# Revit family: КПДУ
name_source: partatom
category: Арматура воздуховодов
units: mm (PartAtom-declared; Revit-internal decimal feet)

## family parameters
Всегда вертикально = Да
На основе рабочей плоскости = Нет
Общий = Нет
При загрузке вырезать с полостями = Нет
Размер круглого соединителя = Использовать диаметр
Тип детали = Присоединяется

## types (184) — shared parameters
00_20_Manufacturer = Вентс
00_20_Name = Клапан протипожежний димовий
Grid Material = Cover Grid Cross
Load Classification = HVAC
Maintenance zone material = <По категории>
Maximum Air Flow = 0.0 л/с
zero-valued in all types: Отметка по умолчанию

## per-type parameters (varying)
| type | 00_20_Type | B | B1 | B2 | B3 | Bn | H | H1 | H2 | H3 | Hn | Power | Voltage | Вес | Два фланца | Количество створок | Размещение привода (внутри) | Размещение привода (снаружи) |
| КПДУ-300х300-2-ПВ24-СН | КПДУ-300х300-2-ПВ24-СН | 300 мм | 320 мм | 340 мм | 160 мм | 310 мм | 300 мм | 320 мм | 340 мм | 50 мм | 310 мм | 9 В·А | 24 В | 6.5 кг | Да | 1 | Нет | Да |
| КПДУ-1400х1400-2-ПВ24-СН | КПДУ-1400х1400-2-ПВ24-СН | 1400 мм | 1430 мм | 1460 мм | 715 мм | 1410 мм | 1400 мм | 1430 мм | 1460 мм | 600 мм | 1410 мм | 18 В·А | 24 В | 52 кг | Да | 5 | Нет | Да |
| КПДУ-300х300-1-ПВ24-СН | КПДУ-300х300-1-ПВ24-СН | 300 мм | 320 мм | 340 мм | 160 мм | 310 мм | 300 мм | 320 мм | 340 мм | 50 мм | 310 мм | 9 В·А | 24 В | 6.5 кг | Нет | 1 | Нет | Да |
| КПДУ-1400х1400-1-ПВ24-СН | КПДУ-1400х1400-1-ПВ24-СН | 1400 мм | 1430 мм | 1460 мм | 715 мм | 1410 мм | 1400 мм | 1430 мм | 1460 мм | 600 мм | 1410 мм | 18 В·А | 24 В | 52 кг | Нет | 5 | Нет | Да |
| КПДУ-300х300-1-ПВ24-ВН | КПДУ-300х300-1-ПВ24-ВН | 300 мм | 320 мм | 340 мм | 160 мм | 310 мм | 300 мм | 320 мм | 340 мм | 50 мм | 310 мм | 9 В·А | 24 В | 6.5 кг | Нет | 1 | Да | Нет |
| КПДУ-300х300-2-ПВ24-ВН | КПДУ-300х300-2-ПВ24-ВН | 300 мм | 320 мм | 340 мм | 160 мм | 310 мм | 300 мм | 320 мм | 340 мм | 50 мм | 310 мм | 9 В·А | 24 В | 6.5 кг | Да | 1 | Да | Нет |
| КПДУ-1400х1400-1-ПВ24-ВН | КПДУ-1400х1400-1-ПВ24-ВН | 1400 мм | 1430 мм | 1460 мм | 715 мм | 1410 мм | 1400 мм | 1430 мм | 1460 мм | 600 мм | 1410 мм | 18 В·А | 24 В | 52 кг | Нет | 5 | Да | Нет |
| КПДУ-1400х1400-2-ПВ24-ВН | КПДУ-1400х1400-2-ПВ24-ВН | 1400 мм | 1430 мм | 1460 мм | 715 мм | 1410 мм | 1400 мм | 1430 мм | 1460 мм | 600 мм | 1410 мм | 18 В·А | 24 В | 52 кг | Да | 5 | Да | Нет |
| КПДУ-300х300-1-ПВ230-ВН | КПДУ-300х300-1-ПВ230-ВН | 300 мм | 320 мм | 340 мм | 160 мм | 310 мм | 300 мм | 320 мм | 340 мм | 50 мм | 310 мм | 12 В·А | 230 В | 6.5 кг | Нет | 1 | Да | Нет |
| КПДУ-300х300-1-ПВ230-СН | КПДУ-300х300-1-ПВ230-СН | 300 мм | 320 мм | 340 мм | 160 мм | 310 мм | 300 мм | 320 мм | 340 мм | 50 мм | 310 мм | 12 В·А | 230 В | 6.5 кг | Нет | 1 | Нет | Да |
| КПДУ-300х300-2-ПВ230-ВН | КПД-300х300-2-ПВ230-ВН | 300 мм | 320 мм | 340 мм | 160 мм | 310 мм | 300 мм | 320 мм | 340 мм | 50 мм | 310 мм | 12 В·А | 230 В | 6.5 кг | Да | 1 | Да | Нет |
| КПДУ-300х300-2-ПВ230-СН | КПДУ-300х300-2-ПВ230-СН | 300 мм | 320 мм | 340 мм | 160 мм | 310 мм | 300 мм | 320 мм | 340 мм | 50 мм | 310 мм | 12 В·А | 230 В | 6.5 кг | Да | 1 | Нет | Да |
| КПДУ-1400х1400-1-ПВ230-ВН | КПДУ-1400х1400-1-ПВ230-ВН | 1400 мм | 1430 мм | 1460 мм | 715 мм | 1410 мм | 1400 мм | 1430 мм | 1460 мм | 600 мм | 1410 мм | 15 В·А | 230 В | 52 кг | Нет | 5 | Да | Нет |
| КПДУ-1400х1400-1-ПВ230-СН | КПДУ-1400х1400-1-ПВ230-СН | 1400 мм | 1430 мм | 1460 мм | 715 мм | 1410 мм | 1400 мм | 1430 мм | 1460 мм | 600 мм | 1410 мм | 15 В·А | 230 В | 52 кг | Нет | 5 | Нет | Да |
| КПДУ-1400х1400-2-ПВ230-ВН | КПДУ-1400х1400-2-ПВ230-ВН | 1400 мм | 1430 мм | 1460 мм | 715 мм | 1410 мм | 1400 мм | 1430 мм | 1460 мм | 600 мм | 1410 мм | 15 В·А | 230 В | 52 кг | Да | 5 | Да | Нет |
| КПДУ-1400х1400-2-ПВ230-СН | КПДУ-1400х1400-2-ПВ230-СН | 1400 мм | 1430 мм | 1460 мм | 715 мм | 1410 мм | 1400 мм | 1430 мм | 1460 мм | 600 мм | 1410 мм | 15 В·А | 230 В | 52 кг | Да | 5 | Нет | Да |
| КПДУ-350х350-1-ПВ230-ВН | КПДУ-350х350-1-ПВ230-ВН | 350 мм | 370 мм | 390 мм | 185 мм | 360 мм | 350 мм | 370 мм | 390 мм | 75 мм | 360 мм | 12 В·А | 230 В | 7.8 кг | Нет | 1 | Да | Нет |
| КПДУ-350х350-1-ПВ230-СН | КПДУ-350х350-1-ПВ230-СН | 350 мм | 370 мм | 390 мм | 185 мм | 360 мм | 350 мм | 370 мм | 390 мм | 75 мм | 360 мм | 12 В·А | 230 В | 7.8 кг | Нет | 1 | Нет | Да |
| КПДУ-350х350-1-ПВ24-ВН | КПДУ-350х350-1-ПВ24-ВН | 350 мм | 370 мм | 390 мм | 185 мм | 360 мм | 350 мм | 370 мм | 390 мм | 75 мм | 360 мм | 9 В·А | 24 В | 7.8 кг | Нет | 1 | Да | Нет |
| КПДУ-350х350-1-ПВ24-СН | КПДУ-350х350-1-ПВ24-СН | 350 мм | 370 мм | 390 мм | 185 мм | 360 мм | 350 мм | 370 мм | 390 мм | 75 мм | 360 мм | 9 В·А | 24 В | 7.8 кг | Нет | 1 | Нет | Да |
| КПДУ-350х350-2-ПВ230-ВН | КПДУ-350х350-2-ПВ230-ВН | 350 мм | 370 мм | 390 мм | 185 мм | 360 мм | 350 мм | 370 мм | 390 мм | 75 мм | 360 мм | 12 В·А | 230 В | 7.8 кг | Да | 1 | Да | Нет |
| КПДУ-350х350-2-ПВ230-СН | КПДУ-350х350-2-ПВ230-СН | 350 мм | 370 мм | 390 мм | 185 мм | 360 мм | 350 мм | 370 мм | 390 мм | 75 мм | 360 мм | 12 В·А | 230 В | 7.8 кг | Да | 1 | Нет | Да |
| КПДУ-350х350-2-ПВ24-ВН | КПДУ-350х350-2-ПВ24-ВН | 350 мм | 370 мм | 390 мм | 185 мм | 360 мм | 350 мм | 370 мм | 390 мм | 75 мм | 360 мм | 9 В·А | 24 В | 7.8 кг | Да | 1 | Да | Нет |
| КПДУ-350х350-2-ПВ24-СН | КПДУ-350х350-2-ПВ24-СН | 350 мм | 370 мм | 390 мм | 185 мм | 360 мм | 350 мм | 370 мм | 390 мм | 75 мм | 360 мм | 9 В·А | 24 В | 7.8 кг | Да | 1 | Нет | Да |
| КПДУ-400х400-1-ПВ230-ВН | КПДУ-400х400-1-ПВ230-ВН | 400 мм | 420 мм | 440 мм | 210 мм | 410 мм | 400 мм | 420 мм | 440 мм | 100 мм | 410 мм | 12 В·А | 230 В | 9.5 кг | Нет | 2 | Да | Нет |
| КПДУ-400х400-1-ПВ230-СН | КПДУ-400х400-1-ПВ230-СН | 400 мм | 420 мм | 440 мм | 210 мм | 410 мм | 400 мм | 420 мм | 440 мм | 100 мм | 410 мм | 12 В·А | 230 В | 9.5 кг | Нет | 2 | Нет | Да |
| КПДУ-400х400-1-ПВ24-СН | КПДУ-400х400-1-ПВ24-СН | 400 мм | 420 мм | 440 мм | 210 мм | 410 мм | 400 мм | 420 мм | 440 мм | 100 мм | 410 мм | 9 В·А | 24 В | 9.5 кг | Нет | 2 | Нет | Да |
| КПДУ-400х400-1-ПВ24-ВН | КПДУ-400х400-1-ПВ24-ВН | 400 мм | 420 мм | 440 мм | 210 мм | 410 мм | 400 мм | 420 мм | 440 мм | 100 мм | 410 мм | 9 В·А | 24 В | 9.5 кг | Нет | 2 | Да | Нет |
| КПДУ-400х400-2-ПВ230-ВН | КПДУ-400х400-2-ПВ230-ВН | 400 мм | 420 мм | 440 мм | 210 мм | 410 мм | 400 мм | 420 мм | 440 мм | 100 мм | 410 мм | 12 В·А | 230 В | 9.5 кг | Да | 2 | Да | Нет |
| КПДУ-400х400-2-ПВ230-СН | КПДУ-400х400-2-ПВ230-СН | 400 мм | 420 мм | 440 мм | 210 мм | 410 мм | 400 мм | 420 мм | 440 мм | 100 мм | 410 мм | 12 В·А | 230 В | 9.5 кг | Да | 2 | Нет | Да |
| КПДУ-400х400-2-ПВ24-ВН | КПДУ-400х400-2-ПВ24-ВН | 400 мм | 420 мм | 440 мм | 210 мм | 410 мм | 400 мм | 420 мм | 440 мм | 100 мм | 410 мм | 9 В·А | 24 В | 9.5 кг | Да | 2 | Да | Нет |
| КПДУ-400х400-2-ПВ24-СН | КПДУ-400х400-2-ПВ24-СН | 400 мм | 420 мм | 440 мм | 210 мм | 410 мм | 400 мм | 420 мм | 440 мм | 100 мм | 410 мм | 9 В·А | 24 В | 9.5 кг | Да | 2 | Нет | Да |
| КПДУ-450х450-1-ПВ230-ВН | КПДУ-450х450-1-ПВ230-ВН | 450 мм | 470 мм | 490 мм | 235 мм | 460 мм | 450 мм | 470 мм | 490 мм | 125 мм | 460 мм | 12 В·А | 230 В | 11.3 кг | Нет | 2 | Да | Нет |
| КПДУ-450х450-1-ПВ230-СН | КПДУ-450х450-1-ПВ230-СН | 450 мм | 470 мм | 490 мм | 235 мм | 460 мм | 450 мм | 470 мм | 490 мм | 125 мм | 460 мм | 12 В·А | 230 В | 11.3 кг | Нет | 2 | Нет | Да |
| КПДУ-450х450-1-ПВ24-ВН | КПДУ-450х450-1-ПВ24-ВН | 450 мм | 470 мм | 490 мм | 235 мм | 460 мм | 450 мм | 470 мм | 490 мм | 125 мм | 460 мм | 9 В·А | 24 В | 11.3 кг | Нет | 2 | Да | Нет |
| КПДУ-450х450-1-ПВ24-СН | КПДУ-450х450-1-ПВ24-СН | 450 мм | 470 мм | 490 мм | 235 мм | 460 мм | 450 мм | 470 мм | 490 мм | 125 мм | 460 мм | 9 В·А | 24 В | 11.3 кг | Нет | 2 | Нет | Да |
| КПДУ-450х450-2-ПВ230-ВН | КПДУ-450х450-2-ПВ230-ВН | 450 мм | 470 мм | 490 мм | 235 мм | 460 мм | 450 мм | 470 мм | 490 мм | 125 мм | 460 мм | 12 В·А | 230 В | 11.3 кг | Да | 2 | Да | Нет |
| КПДУ-450х450-2-ПВ230-СН | КПДУ-450х450-2-ПВ230-СН | 450 мм | 470 мм | 490 мм | 235 мм | 460 мм | 450 мм | 470 мм | 490 мм | 125 мм | 460 мм | 12 В·А | 230 В | 11.3 кг | Да | 2 | Нет | Да |
| КПДУ-450х450-2-ПВ24-ВН | КПДУ-450х450-2-ПВ24-ВН | 450 мм | 470 мм | 490 мм | 235 мм | 460 мм | 450 мм | 470 мм | 490 мм | 125 мм | 460 мм | 9 В·А | 24 В | 11.3 кг | Да | 2 | Да | Нет |
| КПДУ-450х450-2-ПВ24-СН | КПДУ-450х450-2-ПВ24-СН | 450 мм | 470 мм | 490 мм | 235 мм | 460 мм | 450 мм | 470 мм | 490 мм | 125 мм | 460 мм | 9 В·А | 24 В | 11.3 кг | Да | 2 | Нет | Да |
| КПДУ-500х500-1-ПВ230-ВН | КПДУ-500х500-1-ПВ230-ВН | 500 мм | 520 мм | 540 мм | 260 мм | 510 мм | 500 мм | 520 мм | 540 мм | 150 мм | 510 мм | 12 В·А | 230 В | 12.1 кг | Нет | 2 | Да | Нет |
| КПДУ-500х500-1-ПВ230-СН | КПДУ-500х500-1-ПВ230-СН | 500 мм | 520 мм | 540 мм | 260 мм | 510 мм | 500 мм | 520 мм | 540 мм | 150 мм | 510 мм | 12 В·А | 230 В | 12.1 кг | Нет | 2 | Нет | Да |
| КПДУ-500х500-1-ПВ24-ВН | КПДУ-500х500-1-ПВ24-ВН | 500 мм | 520 мм | 540 мм | 260 мм | 510 мм | 500 мм | 520 мм | 540 мм | 150 мм | 510 мм | 9 В·А | 24 В | 12.1 кг | Нет | 2 | Да | Нет |
| КПДУ-500х500-1-ПВ24-СН | КПДУ-500х500-1-ПВ24-СН | 500 мм | 520 мм | 540 мм | 260 мм | 510 мм | 500 мм | 520 мм | 540 мм | 150 мм | 510 мм | 9 В·А | 24 В | 12.1 кг | Нет | 2 | Нет | Да |
| КПДУ-500х500-2-ПВ230-ВН | КПДУ-500х500-2-ПВ230-ВН | 500 мм | 520 мм | 540 мм | 260 мм | 510 мм | 500 мм | 520 мм | 540 мм | 150 мм | 510 мм | 12 В·А | 230 В | 12.1 кг | Да | 2 | Да | Нет |
| КПДУ-500х500-2-ПВ230-СН | КПДУ-500х500-2-ПВ230-СН | 500 мм | 520 мм | 540 мм | 260 мм | 510 мм | 500 мм | 520 мм | 540 мм | 150 мм | 510 мм | 12 В·А | 230 В | 12.1 кг | Да | 2 | Нет | Да |
| КПДУ-500х500-2-ПВ24-ВН | КПДУ-500х500-2-ПВ24-ВН | 500 мм | 520 мм | 540 мм | 260 мм | 510 мм | 500 мм | 520 мм | 540 мм | 150 мм | 510 мм | 9 В·А | 24 В | 12.1 кг | Да | 2 | Да | Нет |
| КПДУ-500х500-2-ПВ24-СН | КПДУ-500х500-2-ПВ24-СН | 500 мм | 520 мм | 540 мм | 260 мм | 510 мм | 500 мм | 520 мм | 540 мм | 150 мм | 510 мм | 9 В·А | 24 В | 12.1 кг | Да | 2 | Нет | Да |
| КПДУ-550х550-1-ПВ230-ВН | КПДУ-550х550-1-ПВ230-ВН | 550 мм | 580 мм | 610 мм | 290 мм | 560 мм | 550 мм | 580 мм | 610 мм | 175 мм | 560 мм | 15 В·А | 230 В | 14.2 кг | Нет | 2 | Да | Нет |
| КПДУ-550х550-1-ПВ230-СН | КПДУ-550х550-1-ПВ230-СН | 550 мм | 580 мм | 610 мм | 290 мм | 560 мм | 550 мм | 580 мм | 610 мм | 175 мм | 560 мм | 15 В·А | 230 В | 14.2 кг | Нет | 2 | Нет | Да |
| КПДУ-550х550-1-ПВ24-ВН | КПДУ-550х550-1-ПВ24-ВН | 550 мм | 580 мм | 610 мм | 290 мм | 560 мм | 550 мм | 580 мм | 610 мм | 175 мм | 560 мм | 18 В·А | 24 В | 14.2 кг | Нет | 2 | Да | Нет |
| КПДУ-550х550-1-ПВ24-СН | КПДУ-550х550-1-ПВ24-СН | 550 мм | 580 мм | 610 мм | 290 мм | 560 мм | 550 мм | 580 мм | 610 мм | 175 мм | 560 мм | 18 В·А | 24 В | 14.2 кг | Нет | 2 | Нет | Да |
| КПДУ-550х550-2-ПВ230-ВН | КПДУ-550х550-2-ПВ230-ВН | 550 мм | 580 мм | 610 мм | 290 мм | 560 мм | 550 мм | 580 мм | 610 мм | 175 мм | 560 мм | 15 В·А | 230 В | 14.2 кг | Да | 2 | Да | Нет |
| КПДУ-550х550-2-ПВ230-СН | КПДУ-550х550-2-ПВ230-СН | 550 мм | 580 мм | 610 мм | 290 мм | 560 мм | 550 мм | 580 мм | 610 мм | 175 мм | 560 мм | 15 В·А | 230 В | 14.2 кг | Да | У | Нет | Да |
| КПДУ-550х550-2-ПВ24-ВН | КПДУ-550х550-2-ПВ24-ВН | 550 мм | 580 мм | 610 мм | 290 мм | 560 мм | 550 мм | 580 мм | 610 мм | 175 мм | 560 мм | 18 В·А | 24 В | 14.2 кг | Да | 2 | Да | Нет |
| КПДУ-550х550-2-ПВ24-СН | КПДУ-550х550-2-ПВ24-СН | 550 мм | 580 мм | 610 мм | 290 мм | 560 мм | 550 мм | 580 мм | 610 мм | 175 мм | 560 мм | 18 В·А | 24 В | 14.2 кг | Да | 2 | Нет | Да |
| КПДУ-600х600-1-ПВ230-ВН | КПДУ-600х600-1-ПВ230-ВН | 600 мм | 630 мм | 660 мм | 315 мм | 610 мм | 600 мм | 630 мм | 660 мм | 200 мм | 610 мм | 15 В·А | 230 В | 17 кг | Нет | 3 | Да | Нет |
| КПДУ-600х600-1-ПВ230-СН | КПДУ-600х600-1-ПВ230-СН | 600 мм | 630 мм | 660 мм | 315 мм | 610 мм | 600 мм | 630 мм | 660 мм | 200 мм | 610 мм | 15 В·А | 230 В | 17 кг | Нет | 3 | Нет | Да |
| КПДУ-600х600-1-ПВ24-ВН | КПДУ-600х600-1-ПВ24-ВН | 600 мм | 630 мм | 660 мм | 315 мм | 610 мм | 600 мм | 630 мм | 660 мм | 200 мм | 610 мм | 18 В·А | 24 В | 17 кг | Нет | 3 | Да | Нет |
| КПДУ-600х600-1-ПВ24-СН | КПДУ-600х600-1-ПВ24-СН | 600 мм | 630 мм | 660 мм | 315 мм | 610 мм | 600 мм | 630 мм | 660 мм | 200 мм | 610 мм | 18 В·А | 24 В | 17 кг | Нет | 3 | Нет | Да |
| КПДУ-600х600-2-ПВ230-ВН | КПДУ-600х600-2-ПВ230-ВН | 600 мм | 630 мм | 660 мм | 315 мм | 610 мм | 600 мм | 630 мм | 660 мм | 200 мм | 610 мм | 15 В·А | 230 В | 17 кг | Да | 3 | Да | Нет |
| КПДУ-600х600-2-ПВ230-СН | КПДУ-600х600-2-ПВ230-СН | 600 мм | 630 мм | 660 мм | 315 мм | 610 мм | 600 мм | 630 мм | 660 мм | 200 мм | 610 мм | 15 В·А | 230 В | 17 кг | Да | 3 | Нет | Да |
| КПДУ-600х600-2-ПВ24-ВН | КПДУ-600х600-2-ПВ24-ВН | 600 мм | 630 мм | 660 мм | 315 мм | 610 мм | 600 мм | 630 мм | 660 мм | 200 мм | 610 мм | 18 В·А | 24 В | 17 кг | Да | 3 | Да | Нет |
| КПДУ-600х600-2-ПВ24-СН | КПДУ-600х600-2-ПВ24-СН | 600 мм | 630 мм | 660 мм | 315 мм | 610 мм | 600 мм | 630 мм | 660 мм | 200 мм | 610 мм | 18 В·А | 24 В | 17 кг | Да | 3 | Нет | Да |
| КПДУ-650х650-1-ПВ230-ВН | КПДУ-650х650-1-ПВ230-ВН | 650 мм | 680 мм | 710 мм | 340 мм | 660 мм | 650 мм | 680 мм | 710 мм | 225 мм | 660 мм | 15 В·А | 230 В | 19 кг | Нет | 3 | Да | Нет |
| КПДУ-650х650-1-ПВ230-СН | КПДУ-650х650-1-ПВ230-СН | 650 мм | 680 мм | 710 мм | 340 мм | 660 мм | 650 мм | 680 мм | 710 мм | 225 мм | 660 мм | 15 В·А | 230 В | 19 кг | Нет | 3 | Нет | Да |
| КПДУ-650х650-1-ПВ24-ВН | КПДУ-650х650-1-ПВ24-ВН | 650 мм | 680 мм | 710 мм | 340 мм | 660 мм | 650 мм | 680 мм | 710 мм | 225 мм | 660 мм | 18 В·А | 24 В | 19 кг | Нет | 3 | Да | Нет |
| КПДУ-650х650-1-ПВ24-СН | КПДУ-650х650-1-ПВ24-СН | 650 мм | 680 мм | 710 мм | 340 мм | 660 мм | 650 мм | 680 мм | 710 мм | 225 мм | 660 мм | 18 В·А | 24 В | 19 кг | Нет | 3 | Нет | Да |
| КПДУ-650х650-2-ПВ230-ВН | КПДУ-650х650-2-ПВ230-ВН | 650 мм | 680 мм | 710 мм | 340 мм | 660 мм | 650 мм | 680 мм | 710 мм | 225 мм | 660 мм | 15 В·А | 230 В | 19 кг | Да | 3 | Да | Нет |
| КПДУ-650х650-2-ПВ230-СН | КПДУ-650х650-2-ПВ230-СН | 650 мм | 680 мм | 710 мм | 340 мм | 660 мм | 650 мм | 680 мм | 710 мм | 225 мм | 660 мм | 15 В·А | 230 В | 19 кг | Да | 3 | Нет | Да |
| КПДУ-650х650-2-ПВ24-ВН | КПДУ-650х650-2-ПВ24-ВН | 650 мм | 680 мм | 710 мм | 340 мм | 660 мм | 650 мм | 680 мм | 710 мм | 225 мм | 660 мм | 18 В·А | 24 В | 19 кг | Да | 3 | Да | Нет |
| КПДУ-650х650-2-ПВ24-СН | КПДУ-650х650-2-ПВ24-СН | 650 мм | 680 мм | 710 мм | 340 мм | 660 мм | 650 мм | 680 мм | 710 мм | 225 мм | 660 мм | 18 В·А | 24 В | 19 кг | Да | 3 | Нет | Да |
| КПДУ-700х700-1-ПВ230-ВН | КПДУ-700х700-1-ПВ230-ВН | 700 мм | 730 мм | 760 мм | 365 мм | 710 мм | 700 мм | 730 мм | 760 мм | 250 мм | 710 мм | 15 В·А | 230 В | 20.3 кг | Нет | 3 | Да | Нет |
| КПДУ-700х700-1-ПВ230-СН | КПДУ-700х700-1-ПВ230-СН | 700 мм | 730 мм | 760 мм | 365 мм | 710 мм | 700 мм | 730 мм | 760 мм | 250 мм | 710 мм | 15 В·А | 230 В | 20.3 кг | Нет | 3 | Нет | Да |
| КПДУ-700х700-1-ПВ24-ВН | КПДУ-700х700-1-ПВ24-ВН | 700 мм | 730 мм | 760 мм | 365 мм | 710 мм | 700 мм | 730 мм | 760 мм | 250 мм | 710 мм | 18 В·А | 24 В | 20.3 кг | Нет | 3 | Да | Нет |
| КПДУ-700х700-1-ПВ24-СН | КПДУ-700х700-1-ПВ24-СН | 700 мм | 730 мм | 760 мм | 365 мм | 710 мм | 700 мм | 730 мм | 760 мм | 250 мм | 710 мм | 18 В·А | 24 В | 20.3 кг | Нет | 3 | Нет | Да |
| КПДУ-700х700-2-ПВ230-ВН | КПДУ-700х700-2-ПВ230-ВН | 700 мм | 730 мм | 760 мм | 365 мм | 710 мм | 700 мм | 730 мм | 760 мм | 250 мм | 710 мм | 15 В·А | 230 В | 20.3 кг | Да | 3 | Да | Нет |
| КПДУ-700х700-2-ПВ230-СН | КПДУ-700х700-2-ПВ230-СН | 700 мм | 730 мм | 760 мм | 365 мм | 710 мм | 700 мм | 730 мм | 760 мм | 250 мм | 710 мм | 15 В·А | 230 В | 20.3 кг | Да | 3 | Нет | Да |
| КПДУ-700х700-2-ПВ24-ВН | КПДУ-700х700-2-ПВ24-ВН | 700 мм | 730 мм | 760 мм | 365 мм | 710 мм | 700 мм | 730 мм | 760 мм | 250 мм | 710 мм | 18 В·А | 24 В | 20.3 кг | Да | 3 | Да | Нет |
| КПДУ-700х700-2-ПВ24-СН | КПДУ-700х700-2-ПВ24-СН | 700 мм | 730 мм | 760 мм | 365 мм | 710 мм | 700 мм | 730 мм | 760 мм | 250 мм | 710 мм | 18 В·А | 24 В | 20.3 кг | Да | 3 | Нет | Да |
| КПДУ-750х750-1-ПВ230-ВН | КПДУ-750х750-1-ПВ230-ВН | 750 мм | 780 мм | 810 мм | 390 мм | 760 мм | 750 мм | 780 мм | 810 мм | 275 мм | 760 мм | 15 В·А | 230 В | 22.1 кг | Нет | 3 | Да | Нет |
| КПДУ-750х750-1-ПВ230-СН | КПДУ-750х750-1-ПВ230-СН | 750 мм | 780 мм | 810 мм | 390 мм | 760 мм | 750 мм | 780 мм | 810 мм | 275 мм | 760 мм | 15 В·А | 230 В | 22.1 кг | Нет | 3 | Нет | Да |
| КПДУ-750х750-1-ПВ24-ВН | КПДУ-750х750-1-ПВ24-ВН | 750 мм | 780 мм | 810 мм | 390 мм | 760 мм | 750 мм | 780 мм | 810 мм | 275 мм | 760 мм | 18 В·А | 24 В | 22.1 кг | Нет | 3 | Да | Нет |
| КПДУ-750х750-1-ПВ24-СН | КПДУ-750х750-1-ПВ24-СН | 750 мм | 780 мм | 810 мм | 390 мм | 760 мм | 750 мм | 780 мм | 810 мм | 275 мм | 760 мм | 18 В·А | 24 В | 22.1 кг | Нет | 3 | Нет | Да |
| КПДУ-750х750-2-ПВ230-ВН | КПДУ-750х750-2-ПВ230-ВН | 750 мм | 780 мм | 810 мм | 390 мм | 760 мм | 750 мм | 780 мм | 810 мм | 275 мм | 760 мм | 15 В·А | 230 В | 22.1 кг | Да | 3 | Да | Нет |
| КПДУ-750х750-2-ПВ230-СН | КПДУ-750х750-2-ПВ230-СН | 750 мм | 780 мм | 810 мм | 390 мм | 760 мм | 750 мм | 780 мм | 810 мм | 275 мм | 760 мм | 15 В·А | 230 В | 22.1 кг | Да | 3 | Нет | Да |
| КПДУ-750х750-2-ПВ24-ВН | КПДУ-750х750-2-ПВ24-ВН | 750 мм | 780 мм | 810 мм | 390 мм | 760 мм | 750 мм | 780 мм | 810 мм | 275 мм | 760 мм | 18 В·А | 24 В | 22.1 кг | Да | 3 | Да | Нет |
| КПДУ-750х750-2-ПВ24-СН | КПДУ-750х750-2-ПВ24-СН | 750 мм | 780 мм | 810 мм | 390 мм | 760 мм | 750 мм | 780 мм | 810 мм | 275 мм | 760 мм | 18 В·А | 24 В | 22.1 кг | Да | 3 | Нет | Да |
| КПДУ-800х800-1-ПВ230-ВН | КПДУ-800х800-1-ПВ230-ВН | 800 мм | 830 мм | 860 мм | 415 мм | 810 мм | 800 мм | 830 мм | 860 мм | 300 мм | 810 мм | 15 В·А | 230 В | 24.8 кг | Нет | 4 | Да | Нет |
| КПДУ-800х800-1-ПВ230-СН | КПДУ-800х800-1-ПВ230-СН | 800 мм | 830 мм | 860 мм | 415 мм | 810 мм | 800 мм | 830 мм | 860 мм | 300 мм | 810 мм | 15 В·А | 230 В | 24.8 кг | Нет | 4 | Нет | Да |
| КПДУ-800х800-1-ПВ24-ВН | КПДУ-800х800-1-ПВ24-ВН | 800 мм | 830 мм | 860 мм | 415 мм | 810 мм | 800 мм | 830 мм | 860 мм | 300 мм | 810 мм | 18 В·А | 24 В | 24.8 кг | Нет | 4 | Да | Нет |
| КПДУ-800х800-1-ПВ24-СН | КПДУ-800х800-1-ПВ24-СН | 800 мм | 830 мм | 860 мм | 415 мм | 810 мм | 800 мм | 830 мм | 860 мм | 300 мм | 810 мм | 18 В·А | 24 В | 24.8 кг | Нет | 4 | Нет | Да |
| КПДУ-800х800-2-ПВ230-ВН | КПДУ-800х800-2-ПВ230-ВН | 800 мм | 830 мм | 860 мм | 415 мм | 810 мм | 800 мм | 830 мм | 860 мм | 300 мм | 810 мм | 15 В·А | 230 В | 24.8 кг | Да | 4 | Да | Нет |
| КПДУ-800х800-2-ПВ230-СН | КПДУ-800х800-2-ПВ230-СН | 800 мм | 830 мм | 860 мм | 415 мм | 810 мм | 800 мм | 830 мм | 860 мм | 300 мм | 810 мм | 15 В·А | 230 В | 24.8 кг | Да | 4 | Нет | Да |
| КПДУ-800х800-2-ПВ24-ВН | КПДУ-800х800-2-ПВ24-ВН | 800 мм | 830 мм | 860 мм | 415 мм | 810 мм | 800 мм | 830 мм | 860 мм | 300 мм | 810 мм | 18 В·А | 24 В | 24.8 кг | Да | 4 | Да | Нет |
| КПДУ-800х800-2-ПВ24-СН | КПДУ-800х800-2-ПВ24-СН | 800 мм | 830 мм | 860 мм | 415 мм | 810 мм | 800 мм | 830 мм | 860 мм | 300 мм | 810 мм | 18 В·А | 24 В | 24.8 кг | Да | 4 | Нет | Да |
| КПДУ-850х850-1-ПВ230-ВН | КПДУ-850х850-1-ПВ230-ВН | 850 мм | 880 мм | 910 мм | 440 мм | 860 мм | 850 мм | 880 мм | 910 мм | 325 мм | 860 мм | 15 В·А | 230 В | 26.8 кг | Нет | 4 | Да | Нет |
| КПДУ-850х850-1-ПВ230-СН | КПДУ-850х850-1-ПВ230-СН | 850 мм | 880 мм | 910 мм | 440 мм | 860 мм | 850 мм | 880 мм | 910 мм | 325 мм | 860 мм | 15 В·А | 230 В | 26.8 кг | Нет | 4 | Нет | Да |
| КПДУ-850х850-1-ПВ24-ВН | КПДУ-850х850-1-ПВ24-ВН | 850 мм | 880 мм | 910 мм | 440 мм | 860 мм | 850 мм | 880 мм | 910 мм | 325 мм | 860 мм | 18 В·А | 24 В | 26.8 кг | Нет | 4 | Да | Нет |
| КПДУ-850х850-1-ПВ24-СН | КПДУ-850х850-1-ПВ24-СН | 850 мм | 880 мм | 910 мм | 440 мм | 860 мм | 850 мм | 880 мм | 910 мм | 325 мм | 860 мм | 18 В·А | 24 В | 26.8 кг | Нет | 4 | Нет | Да |
| КПДУ-850х850-2-ПВ230-ВН | КПДУ-850х850-2-ПВ230-ВН | 850 мм | 880 мм | 910 мм | 440 мм | 860 мм | 850 мм | 880 мм | 910 мм | 325 мм | 860 мм | 15 В·А | 230 В | 26.8 кг | Да | 4 | Да | Нет |
| КПДУ-850х850-2-ПВ230-СН | КПДУ-850х850-2-ПВ230-СН | 850 мм | 880 мм | 910 мм | 440 мм | 860 мм | 850 мм | 880 мм | 910 мм | 325 мм | 860 мм | 15 В·А | 230 В | 26.8 кг | Да | 4 | Нет | Да |
| КПДУ-850х850-2-ПВ24-ВН | КПДУ-850х850-2-ПВ24-ВН | 850 мм | 880 мм | 910 мм | 440 мм | 860 мм | 850 мм | 880 мм | 910 мм | 325 мм | 860 мм | 18 В·А | 24 В | 26.8 кг | Да | 4 | Да | Нет |
| КПДУ-850х850-2-ПВ24-СН | КПДУ-850х850-2-ПВ24-СН | 850 мм | 880 мм | 910 мм | 440 мм | 860 мм | 850 мм | 880 мм | 910 мм | 325 мм | 860 мм | 18 В·А | 24 В | 26.8 кг | Да | 4 | Нет | Да |
| КПДУ-900х900-1-ПВ230-ВН | КПДУ-900х900-1-ПВ230-ВН | 900 мм | 930 мм | 960 мм | 465 мм | 910 мм | 900 мм | 930 мм | 960 мм | 350 мм | 910 мм | 15 В·А | 230 В | 28.8 кг | Нет | 4 | Да | Нет |
| КПДУ-900х900-1-ПВ230-СН | КПДУ-900х900-1-ПВ230-СН | 900 мм | 930 мм | 960 мм | 465 мм | 910 мм | 900 мм | 930 мм | 960 мм | 350 мм | 910 мм | 15 В·А | 230 В | 28.8 кг | Нет | 4 | Нет | Да |
| КПДУ-900х900-1-ПВ24-ВН | КПДУ-900х900-1-ПВ24-ВН | 900 мм | 930 мм | 960 мм | 465 мм | 910 мм | 900 мм | 930 мм | 960 мм | 350 мм | 910 мм | 18 В·А | 24 В | 28.8 кг | Нет | 4 | Да | Нет |
| КПДУ-900х900-1-ПВ24-СН | КПДУ-900х900-1-ПВ24-СН | 900 мм | 930 мм | 960 мм | 465 мм | 910 мм | 900 мм | 930 мм | 960 мм | 350 мм | 910 мм | 18 В·А | 24 В | 28.8 кг | Нет | 4 | Нет | Да |
| КПДУ-900х900-2-ПВ230-ВН | КПДУ-900х900-2-ПВ230-ВН | 900 мм | 930 мм | 960 мм | 465 мм | 910 мм | 900 мм | 930 мм | 960 мм | 350 мм | 910 мм | 15 В·А | 230 В | 28.8 кг | Да | 4 | Да | Нет |
| КПДУ-900х900-2-ПВ230-СН | КПДУ-900х900-2-ПВ230-СН | 900 мм | 930 мм | 960 мм | 465 мм | 910 мм | 900 мм | 930 мм | 960 мм | 350 мм | 910 мм | 15 В·А | 230 В | 28.8 кг | Да | 4 | Нет | Да |
| КПДУ-900х900-2-ПВ24-ВН | КПДУ-900х900-2-ПВ24-ВН | 900 мм | 930 мм | 960 мм | 465 мм | 910 мм | 900 мм | 930 мм | 960 мм | 350 мм | 910 мм | 18 В·А | 24 В | 28.8 кг | Да | 4 | Да | Нет |
| КПДУ-900х900-2-ПВ24-СН | КПДУ-900х900-2-ПВ24-СН | 900 мм | 930 мм | 960 мм | 465 мм | 910 мм | 900 мм | 930 мм | 960 мм | 350 мм | 910 мм | 18 В·А | 24 В | 28.8 кг | Да | 4 | Нет | Да |
| КПДУ-950х950-1-ПВ230-ВН | КПДУ-950х950-1-ПВ230-ВН | 950 мм | 980 мм | 1010 мм | 490 мм | 960 мм | 950 мм | 980 мм | 1010 мм | 375 мм | 960 мм | 15 В·А | 230 В | 30.8 кг | Нет | 4 | Да | Нет |
| КПДУ-950х950-1-ПВ230-СН | КПДУ-950х950-1-ПВ230-СН | 950 мм | 980 мм | 1010 мм | 490 мм | 960 мм | 950 мм | 980 мм | 1010 мм | 375 мм | 960 мм | 15 В·А | 230 В | 30.8 кг | Нет | 4 | Нет | Да |
| КПДУ-950х950-1-ПВ24-ВН | КПДУ-950х950-1-ПВ24-ВН | 950 мм | 980 мм | 1010 мм | 490 мм | 960 мм | 950 мм | 980 мм | 1010 мм | 375 мм | 960 мм | 18 В·А | 24 В | 30.8 кг | Нет | 4 | Да | Нет |
| КПДУ-950х950-1-ПВ24-СН | КПДУ-950х950-1-ПВ24-СН | 950 мм | 980 мм | 1010 мм | 490 мм | 960 мм | 950 мм | 980 мм | 1010 мм | 375 мм | 960 мм | 18 В·А | 24 В | 30.8 кг | Нет | 4 | Нет | Да |
| КПДУ-950х950-2-ПВ230-ВН | КПДУ-950х950-2-ПВ230-ВН | 950 мм | 980 мм | 1010 мм | 490 мм | 960 мм | 950 мм | 980 мм | 1010 мм | 375 мм | 960 мм | 15 В·А | 230 В | 30.8 кг | Да | 4 | Да | Нет |
| КПДУ-950х950-2-ПВ230-СН | КПДУ-950х950-2-ПВ230-СН | 950 мм | 980 мм | 1010 мм | 490 мм | 960 мм | 950 мм | 980 мм | 1010 мм | 375 мм | 960 мм | 15 В·А | 230 В | 30.8 кг | Да | 4 | Нет | Да |
| КПДУ-950х950-2-ПВ24-ВН | КПДУ-950х950-2-ПВ24-ВН | 950 мм | 980 мм | 1010 мм | 490 мм | 960 мм | 950 мм | 980 мм | 1010 мм | 375 мм | 960 мм | 18 В·А | 24 В | 30.8 кг | Да | 4 | Да | Нет |
| КПДУ-950х950-2-ПВ24-СН | КПДУ-950х950-2-ПВ24-СН | 950 мм | 980 мм | 1010 мм | 490 мм | 960 мм | 950 мм | 980 мм | 1010 мм | 375 мм | 960 мм | 18 В·А | 24 В | 30.8 кг | Да | 4 | Нет | Да |
| КПДУ-1000х1000-1-ПВ230-ВН | КПДУ-1000х1000-1-ПВ230-ВН | 1000 мм | 1030 мм | 1060 мм | 515 мм | 1010 мм | 1000 мм | 1030 мм | 1060 мм | 400 мм | 1010 мм | 15 В·А | 230 В | 32.8 кг | Нет | 4 | Да | Нет |
| КПДУ-1000х1000-1-ПВ230-СН | КПДУ-1000х1000-1-ПВ230-СН | 1000 мм | 1030 мм | 1060 мм | 515 мм | 1010 мм | 1000 мм | 1030 мм | 1060 мм | 400 мм | 1010 мм | 15 В·А | 230 В | 32.8 кг | Нет | 4 | Нет | Да |
| КПДУ-1000х1000-1-ПВ24-ВН | КПДУ1000х1000-1-ПВ24-ВН | 1000 мм | 1030 мм | 1060 мм | 515 мм | 1010 мм | 1000 мм | 1030 мм | 1060 мм | 400 мм | 1010 мм | 18 В·А | 24 В | 32.8 кг | Нет | 4 | Да | Нет |
| КПДУ-1000х1000-1-ПВ24-СН | КПДУ-1000х1000-1-ПВ24-СН | 1000 мм | 1030 мм | 1060 мм | 515 мм | 1010 мм | 1000 мм | 1030 мм | 1060 мм | 400 мм | 1010 мм | 18 В·А | 24 В | 32.8 кг | Нет | 4 | Нет | Да |
| КПДУ-1000х1000-2-ПВ230-ВН | КПДУ-1000х1000-2-ПВ230-ВН | 1000 мм | 1030 мм | 1060 мм | 515 мм | 1010 мм | 1000 мм | 1030 мм | 1060 мм | 400 мм | 1010 мм | 15 В·А | 230 В | 32.8 кг | Да | 4 | Да | Нет |
| КПДУ-1000х1000-2-ПВ230-СН | КПДУ-1000х1000-2-ПВ230-СН | 1000 мм | 1030 мм | 1060 мм | 515 мм | 1010 мм | 1000 мм | 1030 мм | 1060 мм | 400 мм | 1010 мм | 15 В·А | 230 В | 32.8 кг | Да | 4 | Нет | Да |
| КПДУ-1000х1000-2-ПВ24-ВН | КПДУ-1000х1000-2-ПВ24-ВН | 1000 мм | 1030 мм | 1060 мм | 515 мм | 1010 мм | 1000 мм | 1030 мм | 1060 мм | 400 мм | 1010 мм | 18 В·А | 24 В | 32.8 кг | Да | 4 | Да | Нет |
| КПДУ-1000х1000-2-ПВ24-СН | КПДУ-1000х1000-2-ПВ24-СН | 1000 мм | 1030 мм | 1060 мм | 515 мм | 1010 мм | 1000 мм | 1030 мм | 1060 мм | 400 мм | 1010 мм | 18 В·А | 24 В | 32.8 кг | Да | 4 | Нет | Да |
| КПДУ-1050х1050-1-ПВ230-ВН | КПДУ-1050х1050-1-ПВ230-ВН | 1050 мм | 1080 мм | 1110 мм | 540 мм | 1060 мм | 1050 мм | 1080 мм | 1110 мм | 425 мм | 1060 мм | 15 В·А | 230 В | 34.8 кг | Нет | 4 | Да | Нет |
| КПДУ-1050х1050-1-ПВ230-СН | КПДУ-1050х1050-1-ПВ230-СН | 1050 мм | 1080 мм | 1110 мм | 540 мм | 1060 мм | 1050 мм | 1080 мм | 1110 мм | 425 мм | 1060 мм | 15 В·А | 230 В | 34.8 кг | Нет | 4 | Нет | Да |
| КПДУ-1050х1050-1-ПВ24-ВН | КПДУ-1050х1050-1-ПВ24-ВН | 1050 мм | 1080 мм | 1110 мм | 540 мм | 1060 мм | 1050 мм | 1080 мм | 1110 мм | 425 мм | 1060 мм | 18 В·А | 24 В | 34.8 кг | Нет | 4 | Да | Нет |
| КПДУ-1050х1050-1-ПВ24-СН | КПДУ-1050х1050-1-ПВ24-СН | 1050 мм | 1080 мм | 1110 мм | 540 мм | 1060 мм | 1050 мм | 1080 мм | 1110 мм | 425 мм | 1060 мм | 18 В·А | 24 В | 34.8 кг | Нет | 4 | Нет | Да |
| КПДУ-1050х1050-2-ПВ230-ВН | КПДУ-1050х1050-2-ПВ230-ВН | 1050 мм | 1080 мм | 1110 мм | 540 мм | 1060 мм | 1050 мм | 1080 мм | 1110 мм | 425 мм | 1060 мм | 15 В·А | 230 В | 34.8 кг | Да | 4 | Да | Нет |
| КПДУ-1050х1050-2-ПВ230-СН | КПДУ-1050х1050-2-ПВ230-СН | 1050 мм | 1080 мм | 1110 мм | 540 мм | 1060 мм | 1050 мм | 1080 мм | 1110 мм | 425 мм | 1060 мм | 15 В·А | 230 В | 34.8 кг | Да | 4 | Нет | Да |
| КПДУ-1050х1050-2-ПВ24-ВН | КПДУ-1050х1050-2-ПВ24-ВН | 1050 мм | 1080 мм | 1110 мм | 540 мм | 1060 мм | 1050 мм | 1080 мм | 1110 мм | 425 мм | 1060 мм | 18 В·А | 24 В | 34.8 кг | Да | 4 | Да | Нет |
| КПДУ-1050х1050-2-ПВ24-СН | КПДУ-1050х1050-2-ПВ24-СН | 1050 мм | 1080 мм | 1110 мм | 540 мм | 1060 мм | 1050 мм | 1080 мм | 1110 мм | 425 мм | 1060 мм | 18 В·А | 24 В | 34.8 кг | Да | 4 | Нет | Да |
| КПДУ-1100х1100-1-ПВ230-ВН | КПДУ-1100х1100-1-ПВ230-ВН | 1100 мм | 1130 мм | 1160 мм | 565 мм | 1110 мм | 1100 мм | 1130 мм | 1160 мм | 450 мм | 1110 мм | 15 В·А | 230 В | 36.8 кг | Нет | 4 | Да | Нет |
| КПДУ-1100х1100-1-ПВ230-СН | КПДУ-1100х1100-1-ПВ230-СН | 1100 мм | 1130 мм | 1160 мм | 565 мм | 1110 мм | 1100 мм | 1130 мм | 1160 мм | 450 мм | 1110 мм | 15 В·А | 230 В | 36.8 кг | Нет | 4 | Нет | Да |
| КПДУ-1100х1100-1-ПВ24-ВН | КПДУ-1100х1100-1-ПВ24-ВН | 1100 мм | 1130 мм | 1160 мм | 565 мм | 1110 мм | 1100 мм | 1130 мм | 1160 мм | 450 мм | 1110 мм | 18 В·А | 24 В | 36.8 кг | Нет | 4 | Да | Нет |
| КПДУ-1100х1100-1-ПВ24-СН | КПДУ-1100х1100-1-ПВ24-СН | 1100 мм | 1130 мм | 1160 мм | 565 мм | 1110 мм | 1100 мм | 1130 мм | 1160 мм | 450 мм | 1110 мм | 18 В·А | 24 В | 36.8 кг | Нет | 4 | Нет | Да |
| КПДУ-1100х1100-2-ПВ230-ВН | КПДУ-1100х1100-2-ПВ230-ВН | 1100 мм | 1130 мм | 1160 мм | 565 мм | 1110 мм | 1100 мм | 1130 мм | 1160 мм | 450 мм | 1110 мм | 15 В·А | 230 В | 36.8 кг | Да | 4 | Да | Нет |
| КПДУ-1100х1100-2-ПВ230-СН | КПДУ-1100х1100-2-ПВ230-СН | 1100 мм | 1130 мм | 1160 мм | 565 мм | 1110 мм | 1100 мм | 1130 мм | 1160 мм | 450 мм | 1110 мм | 15 В·А | 230 В | 36.8 кг | Да | 4 | Нет | Да |
| КПДУ-1100х1100-2-ПВ24-ВН | КПДУ-1100х1100-2-ПВ24-ВН | 1100 мм | 1130 мм | 1160 мм | 565 мм | 1110 мм | 1100 мм | 1130 мм | 1160 мм | 450 мм | 1110 мм | 18 В·А | 24 В | 36.8 кг | Да | 4 | Да | Нет |
| КПДУ-1100х1100-2-ПВ24-СН | КПДУ-1100х1100-2-ПВ24-СН | 1100 мм | 1130 мм | 1160 мм | 565 мм | 1110 мм | 1100 мм | 1130 мм | 1160 мм | 450 мм | 1110 мм | 18 В·А | 24 В | 36.8 кг | Да | 4 | Нет | Да |
| КПДУ-1150х1150-1-ПВ230-ВН | КПДУ-1150х1150-1-ПВ230-ВН | 1150 мм | 1180 мм | 1210 мм | 590 мм | 1160 мм | 1150 мм | 1180 мм | 1210 мм | 475 мм | 1160 мм | 15 В·А | 230 В | 38.8 кг | Нет | 4 | Да | Нет |
| КПДУ-1150х1150-1-ПВ230-СН | КПДУ-1150х1150-1-ПВ230-СН | 1150 мм | 1180 мм | 1210 мм | 590 мм | 1160 мм | 1150 мм | 1180 мм | 1210 мм | 475 мм | 1160 мм | 15 В·А | 230 В | 38.8 кг | Нет | 4 | Нет | Да |
| КПДУ-1150х1150-1-ПВ24-ВН | КПДУ-1150х1150-1-ПВ24-ВН | 1150 мм | 1180 мм | 1210 мм | 590 мм | 1160 мм | 1150 мм | 1180 мм | 1210 мм | 475 мм | 1160 мм | 18 В·А | 24 В | 38.8 кг | Нет | 4 | Да | Нет |
| КПДУ-1150х1150-1-ПВ24-СН | КПДУ-1150х1150-1-ПВ24-СН | 1150 мм | 1180 мм | 1210 мм | 590 мм | 1160 мм | 1150 мм | 1180 мм | 1210 мм | 475 мм | 1160 мм | 18 В·А | 24 В | 38.8 кг | Нет | 4 | Нет | Да |
| КПДУ-1150х1150-2-ПВ230-ВН | КПДУ-1150х1150-2-ПВ230-ВН | 1150 мм | 1180 мм | 1210 мм | 590 мм | 1160 мм | 1150 мм | 1180 мм | 1210 мм | 475 мм | 1160 мм | 15 В·А | 230 В | 38.8 кг | Да | 4 | Да | Нет |
| КПДУ-1150х1150-2-ПВ230-СН | КПДУ-1150х1150-2-ПВ230-СН | 1150 мм | 1180 мм | 1210 мм | 590 мм | 1160 мм | 1150 мм | 1180 мм | 1210 мм | 475 мм | 1160 мм | 15 В·А | 230 В | 38.8 кг | Да | 4 | Нет | Да |
| КПДУ-1150х1150-2-ПВ24-ВН | КПДУ-1150х1150-2-ПВ24-ВН | 1150 мм | 1180 мм | 1210 мм | 590 мм | 1160 мм | 1150 мм | 1180 мм | 1210 мм | 475 мм | 1160 мм | 18 В·А | 24 В | 38.8 кг | Да | 4 | Да | Нет |
| КПДУ-1150х1150-2-ПВ24-СН | КПДУ-1150х1150-2-ПВ24-СН | 1150 мм | 1180 мм | 1210 мм | 590 мм | 1160 мм | 1150 мм | 1180 мм | 1210 мм | 475 мм | 1160 мм | 18 В·А | 24 В | 38.8 кг | Да | 4 | Нет | Да |
| КПДУ-1200х1200-1-ПВ230-ВН | КПДУ-1200х1200-1-ПВ230-ВН | 1200 мм | 1230 мм | 1260 мм | 615 мм | 1210 мм | 1200 мм | 1230 мм | 1260 мм | 500 мм | 1210 мм | 15 В·А | 230 В | 40.8 кг | Нет | 4 | Да | Нет |
| КПДУ-1200х1200-1-ПВ230-СН | КПДУ-1200х1200-1-ПВ230-СН | 1200 мм | 1230 мм | 1260 мм | 615 мм | 1210 мм | 1200 мм | 1230 мм | 1260 мм | 500 мм | 1210 мм | 15 В·А | 230 В | 40.8 кг | Нет | 4 | Нет | Да |
| КПДУ-1200х1200-1-ПВ24-ВН | КПДУ-1200х1200-1-ПВ24-ВН | 1200 мм | 1230 мм | 1260 мм | 615 мм | 1210 мм | 1200 мм | 1230 мм | 1260 мм | 500 мм | 1210 мм | 18 В·А | 24 В | 40.8 кг | Нет | 4 | Да | Нет |
| КПДУ-1200х1200-1-ПВ24-СН | КПДУ-1200х1200-1-ПВ24-СН | 1200 мм | 1230 мм | 1260 мм | 615 мм | 1210 мм | 1200 мм | 1230 мм | 1260 мм | 500 мм | 1210 мм | 18 В·А | 24 В | 40.8 кг | Нет | 4 | Нет | Да |
| КПДУ-1200х1200-2-ПВ230-ВН | КПДУ-1200х1200-2-ПВ230-ВН | 1200 мм | 1230 мм | 1260 мм | 615 мм | 1210 мм | 1200 мм | 1230 мм | 1260 мм | 500 мм | 1210 мм | 15 В·А | 230 В | 40.8 кг | Да | 4 | Да | Нет |
| КПДУ-1200х1200-2-ПВ230-СН | КПДУ-1200х1200-2-ПВ230-СН | 1200 мм | 1230 мм | 1260 мм | 615 мм | 1210 мм | 1200 мм | 1230 мм | 1260 мм | 500 мм | 1210 мм | 15 В·А | 230 В | 40.8 кг | Да | 4 | Нет | Да |
| КПДУ-1200х1200-2-ПВ24-ВН | КПДУ-1200х1200-2-ПВ24-ВН | 1200 мм | 1230 мм | 1260 мм | 615 мм | 1210 мм | 1200 мм | 1230 мм | 1260 мм | 500 мм | 1210 мм | 18 В·А | 24 В | 40.8 кг | Да | 4 | Да | Нет |
| КПДУ-1200х1200-2-ПВ24-СН | КПДУ-1200х1200-2-ПВ24-СН | 1200 мм | 1230 мм | 1260 мм | 615 мм | 1210 мм | 1200 мм | 1230 мм | 1260 мм | 500 мм | 1210 мм | 18 В·А | 24 В | 40.8 кг | Да | 4 | Нет | Да |
| КПДУ-1250х1250-1-ПВ230-ВН | КПДУ-1250х1250-1-ПВ230-ВН | 1250 мм | 1280 мм | 1310 мм | 640 мм | 1260 мм | 1250 мм | 1280 мм | 1310 мм | 525 мм | 1260 мм | 15 В·А | 230 В | 42.8 кг | Нет | 4 | Да | Нет |
| КПДУ-1250х1250-1-ПВ230-СН | КПДУ-1250х1250-1-ПВ230-СН | 1250 мм | 1280 мм | 1310 мм | 640 мм | 1260 мм | 1250 мм | 1280 мм | 1310 мм | 525 мм | 1260 мм | 15 В·А | 230 В | 42.8 кг | Нет | 4 | Нет | Да |
| КПДУ-1250х1250-1-ПВ24-ВН | КПДУ-1250х1250-1-ПВ24-ВН | 1250 мм | 1280 мм | 1310 мм | 640 мм | 1260 мм | 1250 мм | 1280 мм | 1310 мм | 525 мм | 1260 мм | 18 В·А | 24 В | 42.8 кг | Нет | 4 | Да | Нет |
| КПДУ-1250х1250-1-ПВ24-СН | КПДУ-1250х1250-1-ПВ24-СН | 1250 мм | 1280 мм | 1310 мм | 640 мм | 1260 мм | 1250 мм | 1280 мм | 1310 мм | 525 мм | 1260 мм | 18 В·А | 24 В | 42.8 кг | Нет | 4 | Нет | Да |
| КПДУ-1250х1250-2-ПВ230-ВН | КПДУ-1250х1250-2-ПВ230-ВН | 1250 мм | 1280 мм | 1310 мм | 640 мм | 1260 мм | 1250 мм | 1280 мм | 1310 мм | 525 мм | 1260 мм | 15 В·А | 230 В | 42.8 кг | Да | 4 | Да | Нет |
| КПДУ-1250х1250-2-ПВ230-СН | КПДУ-1250х1250-2-ПВ230-СН | 1250 мм | 1280 мм | 1310 мм | 640 мм | 1260 мм | 1250 мм | 1280 мм | 1310 мм | 525 мм | 1260 мм | 15 В·А | 230 В | 42.8 кг | Да | 4 | Нет | Да |
| КПДУ-1250х1250-2-ПВ24-ВН | КПДУ-1250х1250-2-ПВ24-ВН | 1250 мм | 1280 мм | 1310 мм | 640 мм | 1260 мм | 1250 мм | 1280 мм | 1310 мм | 525 мм | 1260 мм | 18 В·А | 24 В | 42.8 кг | Да | 4 | Да | Нет |
| КПДУ-1250х1250-2-ПВ24-СН | КПДУ-1250х1250-2-ПВ24-СН | 1250 мм | 1280 мм | 1310 мм | 640 мм | 1260 мм | 1250 мм | 1280 мм | 1310 мм | 525 мм | 1260 мм | 18 В·А | 24 В | 42.8 кг | Да | 4 | Нет | Да |
| КПДУ-1300х1300-1-ПВ230-ВН | КПДУ-1300х1300-1-ПВ230-ВН | 1300 мм | 1330 мм | 1360 мм | 665 мм | 1310 мм | 1300 мм | 1330 мм | 1360 мм | 550 мм | 1310 мм | 15 В·А | 230 В | 46 кг | Нет | 5 | Да | Нет |
| КПДУ-1300х1300-1-ПВ230-СН | КПДУ-1300х1300-1-ПВ230-СН | 1300 мм | 1330 мм | 1360 мм | 665 мм | 1310 мм | 1300 мм | 1330 мм | 1360 мм | 550 мм | 1310 мм | 15 В·А | 230 В | 46 кг | Нет | 5 | Нет | Да |
| КПДУ-1300х1300-1-ПВ24-ВН | КПДУ-1300х1300-1-ПВ24-ВН | 1300 мм | 1330 мм | 1360 мм | 665 мм | 1310 мм | 1300 мм | 1330 мм | 1360 мм | 550 мм | 1310 мм | 18 В·А | 24 В | 46 кг | Нет | 5 | Да | Нет |
| КПДУ-1300х1300-1-ПВ24-СН | КПДУ-1300х1300-1-ПВ24-СН | 1300 мм | 1330 мм | 1360 мм | 665 мм | 1310 мм | 1300 мм | 1330 мм | 1360 мм | 550 мм | 1310 мм | 18 В·А | 24 В | 46 кг | Нет | 5 | Нет | Да |
| КПДУ-1300х1300-2-ПВ230-ВН | КПДУ-1300х1300-2-ПВ230-ВН | 1300 мм | 1330 мм | 1360 мм | 665 мм | 1310 мм | 1300 мм | 1330 мм | 1360 мм | 550 мм | 1310 мм | 15 В·А | 230 В | 46 кг | Да | 5 | Да | Нет |
| КПДУ-1300х1300-2-ПВ230-СН | КПДУ-1300х1300-2-ПВ230-СН | 1300 мм | 1330 мм | 1360 мм | 665 мм | 1310 мм | 1300 мм | 1330 мм | 1360 мм | 550 мм | 1310 мм | 15 В·А | 230 В | 46 кг | Да | 5 | Нет | Да |
| КПДУ-1300х1300-2-ПВ24-ВН | КПДУ-1300х1300-2-ПВ24-ВН | 1300 мм | 1330 мм | 1360 мм | 665 мм | 1310 мм | 1300 мм | 1330 мм | 1360 мм | 550 мм | 1310 мм | 18 В·А | 24 В | 46 кг | Да | 5 | Да | Нет |
| КПДУ-1300х1300-2-ПВ24-СН | КПДУ-1300х1300-2-ПВ24-СН | 1300 мм | 1330 мм | 1360 мм | 665 мм | 1310 мм | 1300 мм | 1330 мм | 1360 мм | 550 мм | 1310 мм | 18 В·А | 24 В | 46 кг | Да | 5 | Нет | Да |
| КПДУ-1350х1350-1-ПВ230-ВН | КПДУ-1350х1350-1-ПВ230-ВН | 1350 мм | 1380 мм | 1410 мм | 690 мм | 1360 мм | 1350 мм | 1380 мм | 1410 мм | 575 мм | 1360 мм | 15 В·А | 230 В | 49 кг | Нет | 5 | Да | Нет |
| КПДУ-1350х1350-1-ПВ230-СН | КПДУ-1350х1350-1-ПВ230-СН | 1350 мм | 1380 мм | 1410 мм | 690 мм | 1360 мм | 1350 мм | 1380 мм | 1410 мм | 575 мм | 1360 мм | 15 В·А | 230 В | 49 кг | Нет | 5 | Нет | Да |
| КПДУ-1350х1350-1-ПВ24-ВН | КПДУ-1350х1350-1-ПВ24-ВН | 1350 мм | 1380 мм | 1410 мм | 690 мм | 1360 мм | 1350 мм | 1380 мм | 1410 мм | 575 мм | 1360 мм | 18 В·А | 24 В | 49 кг | Нет | 5 | Да | Нет |
| КПДУ-1350х1350-1-ПВ24-СН | КПДУ-1350х1350-1-ПВ24-СН | 1350 мм | 1380 мм | 1410 мм | 690 мм | 1360 мм | 1350 мм | 1380 мм | 1410 мм | 575 мм | 1360 мм | 18 В·А | 24 В | 49 кг | Нет | 5 | Нет | Да |
| КПДУ-1350х1350-2-ПВ230-ВН | КПДУ-1350х1350-2-ПВ230-ВН | 1350 мм | 1380 мм | 1410 мм | 690 мм | 1360 мм | 1350 мм | 1380 мм | 1410 мм | 575 мм | 1360 мм | 15 В·А | 230 В | 49 кг | Да | 5 | Да | Нет |
| КПДУ-1350х1350-2-ПВ230-СН | КПДУ-1350х1350-2-ПВ230-СН | 1350 мм | 1380 мм | 1410 мм | 690 мм | 1360 мм | 1350 мм | 1380 мм | 1410 мм | 575 мм | 1360 мм | 15 В·А | 230 В | 49 кг | Да | 5 | Нет | Да |
| КПДУ-1350х1350-2-ПВ24-ВН | КПДУ-1350х1350-2-ПВ24-ВН | 1350 мм | 1380 мм | 1410 мм | 690 мм | 1360 мм | 1350 мм | 1380 мм | 1410 мм | 575 мм | 1360 мм | 18 В·А | 24 В | 49 кг | Да | 5 | Да | Нет |
| КПДУ-1350х1350-2-ПВ24-СН | КПДУ-1350х1350-2-ПВ24-СН | 1350 мм | 1380 мм | 1410 мм | 690 мм | 1360 мм | 1350 мм | 1380 мм | 1410 мм | 575 мм | 1360 мм | 18 В·А | 24 В | 49 кг | Да | 5 | Нет | Да |

## geometry (parser evidence)
native form markers: Blend x2
no freeform markers — native parametric forms only
